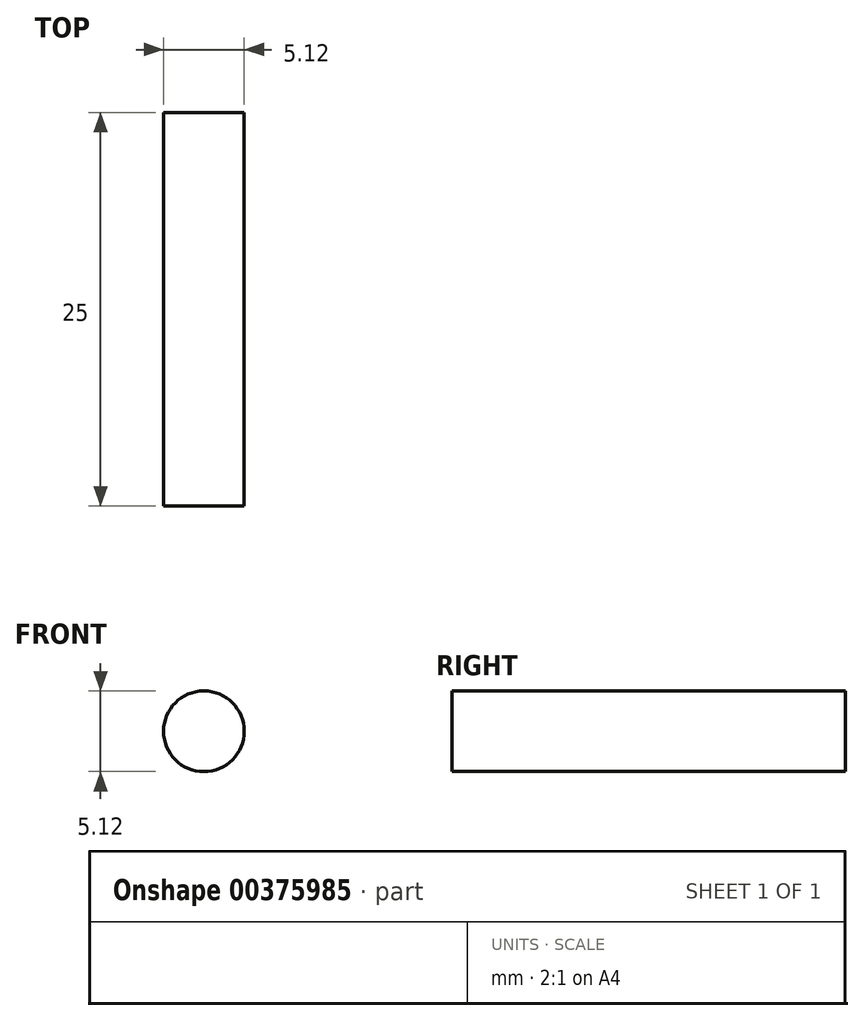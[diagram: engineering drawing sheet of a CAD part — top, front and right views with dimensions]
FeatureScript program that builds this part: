
annotation { "Feature Type Name" : "Feature", "Feature Type Description" : "" }
export const myFeature = defineFeature(function(context is Context, id is Id, definition is map)
    precondition{}
    {
        {
            var Q0;
            Q0=qCreatedBy(makeId("Front.planeOp"),FACE);
            var sketch = newSketch(context, id + "F0", { "sketchPlane" : qUnion([Q0])});
            skCircle(sketch, "E0", {"center": v(0, 0) * mm, "radius": 2.56 * mm});
            skArc(sketch, "E1", {"start": v(-1.68, -4.43) * mm, "mid": v(-2.88, -4.66) * mm, "end": v(-3.9, -5.34) * mm});
            skLineSegment(sketch, "E2", {"start": v(-1.68, -4.42) * mm, "end": v(1.68, -4.42) * mm});
            skArc(sketch, "E3", {"start": v(3.9, -5.34) * mm, "mid": v(2.88, -4.66) * mm, "end": v(1.68, -4.43) * mm});
            skLineSegment(sketch, "E4", {"start": v(3.9, -5.34) * mm, "end": v(7.07, -8.5) * mm});
            skArc(sketch, "E5", {"start": v(6.32, -10.32) * mm, "mid": v(7.3, -9.67) * mm, "end": v(7.07, -8.5) * mm});
            skLineSegment(sketch, "E6", {"start": v(6.32, -10.33) * mm, "end": v(4.22, -10.33) * mm});
            skArc(sketch, "E7", {"start": v(4.22, -10.32) * mm, "mid": v(3.49, -10.63) * mm, "end": v(3.19, -11.36) * mm});
            skLineSegment(sketch, "E8", {"start": v(3.19, -11.36) * mm, "end": v(3.19, -11.47) * mm});
            skArc(sketch, "E9", {"start": v(3.19, -11.47) * mm, "mid": v(3.49, -12.2) * mm, "end": v(4.22, -12.5) * mm});
            skLineSegment(sketch, "E10", {"start": v(4.22, -12.5) * mm, "end": v(5.23, -12.5) * mm});
            skArc(sketch, "E11", {"start": v(6.23, -12.5) * mm, "mid": v(5.73, -12) * mm, "end": v(5.23, -12.5) * mm});
            skLineSegment(sketch, "E12", {"start": v(6.23, -12.5) * mm, "end": v(9.4, -12.5) * mm});
            skArc(sketch, "E13", {"start": v(10.4, -12.5) * mm, "mid": v(9.9, -12) * mm, "end": v(9.4, -12.5) * mm});
            skArc(sketch, "E14", {"start": v(10.4, -12.5) * mm, "mid": v(11.9, -11.9) * mm, "end": v(12.5, -10.4) * mm});
            skArc(sketch, "E15", {"start": v(12.5, -9.4) * mm, "mid": v(12, -9.9) * mm, "end": v(12.5, -10.4) * mm});
            skLineSegment(sketch, "E16", {"start": v(12.5, -9.4) * mm, "end": v(12.5, -6.23) * mm});
            skArc(sketch, "E17", {"start": v(12.5, -5.23) * mm, "mid": v(12, -5.73) * mm, "end": v(12.5, -6.23) * mm});
            skLineSegment(sketch, "E18", {"start": v(12.5, -5.23) * mm, "end": v(12.5, -4.22) * mm});
            skArc(sketch, "E19", {"start": v(12.5, -4.22) * mm, "mid": v(12.2, -3.49) * mm, "end": v(11.47, -3.19) * mm});
            skLineSegment(sketch, "E20", {"start": v(11.47, -3.19) * mm, "end": v(11.36, -3.19) * mm});
            skArc(sketch, "E21", {"start": v(11.36, -3.19) * mm, "mid": v(10.63, -3.49) * mm, "end": v(10.32, -4.22) * mm});
            skLineSegment(sketch, "E22", {"start": v(10.33, -4.22) * mm, "end": v(10.33, -6.3) * mm});
            skArc(sketch, "E23", {"start": v(8.6, -7.02) * mm, "mid": v(9.7, -7.24) * mm, "end": v(10.33, -6.3) * mm});
            skLineSegment(sketch, "E24", {"start": v(8.6, -7.02) * mm, "end": v(5.36, -3.78) * mm});
            skArc(sketch, "E25", {"start": v(4.44, -1.57) * mm, "mid": v(4.68, -2.77) * mm, "end": v(5.36, -3.78) * mm});
            skLineSegment(sketch, "E26", {"start": v(4.44, -1.57) * mm, "end": v(4.44, 1.57) * mm});
            skArc(sketch, "E27", {"start": v(5.36, 3.78) * mm, "mid": v(4.68, 2.77) * mm, "end": v(4.44, 1.57) * mm});
            skLineSegment(sketch, "E28", {"start": v(5.36, 3.78) * mm, "end": v(8.6, 7.02) * mm});
            skArc(sketch, "E29", {"start": v(10.33, 6.3) * mm, "mid": v(9.7, 7.24) * mm, "end": v(8.6, 7.02) * mm});
            skLineSegment(sketch, "E30", {"start": v(10.33, 6.3) * mm, "end": v(10.33, 4.22) * mm});
            skArc(sketch, "E31", {"start": v(10.32, 4.22) * mm, "mid": v(10.63, 3.49) * mm, "end": v(11.36, 3.19) * mm});
            skLineSegment(sketch, "E32", {"start": v(11.36, 3.19) * mm, "end": v(11.47, 3.19) * mm});
            skArc(sketch, "E33", {"start": v(11.47, 3.19) * mm, "mid": v(12.2, 3.49) * mm, "end": v(12.5, 4.22) * mm});
            skLineSegment(sketch, "E34", {"start": v(12.5, 4.22) * mm, "end": v(12.5, 5.23) * mm});
            skArc(sketch, "E35", {"start": v(12.5, 6.23) * mm, "mid": v(12, 5.73) * mm, "end": v(12.5, 5.23) * mm});
            skLineSegment(sketch, "E36", {"start": v(12.5, 6.23) * mm, "end": v(12.5, 9.4) * mm});
            skArc(sketch, "E37", {"start": v(12.5, 10.4) * mm, "mid": v(12, 9.9) * mm, "end": v(12.5, 9.4) * mm});
            skArc(sketch, "E38", {"start": v(12.5, 10.4) * mm, "mid": v(11.9, 11.9) * mm, "end": v(10.4, 12.5) * mm});
            skArc(sketch, "E39", {"start": v(9.4, 12.5) * mm, "mid": v(9.9, 12) * mm, "end": v(10.4, 12.5) * mm});
            skLineSegment(sketch, "E40", {"start": v(9.4, 12.5) * mm, "end": v(6.23, 12.5) * mm});
            skArc(sketch, "E41", {"start": v(5.23, 12.5) * mm, "mid": v(5.73, 12) * mm, "end": v(6.23, 12.5) * mm});
            skLineSegment(sketch, "E42", {"start": v(5.23, 12.5) * mm, "end": v(4.22, 12.5) * mm});
            skArc(sketch, "E43", {"start": v(4.22, 12.5) * mm, "mid": v(3.49, 12.2) * mm, "end": v(3.19, 11.47) * mm});
            skLineSegment(sketch, "E44", {"start": v(3.19, 11.47) * mm, "end": v(3.19, 11.36) * mm});
            skArc(sketch, "E45", {"start": v(3.19, 11.36) * mm, "mid": v(3.49, 10.63) * mm, "end": v(4.22, 10.32) * mm});
            skLineSegment(sketch, "E46", {"start": v(4.22, 10.33) * mm, "end": v(6.37, 10.33) * mm});
            skArc(sketch, "E47", {"start": v(7.1, 8.59) * mm, "mid": v(7.32, 9.7) * mm, "end": v(6.37, 10.32) * mm});
            skLineSegment(sketch, "E48", {"start": v(7.1, 8.59) * mm, "end": v(3.84, 5.34) * mm});
            skArc(sketch, "E49", {"start": v(1.63, 4.43) * mm, "mid": v(2.82, 4.66) * mm, "end": v(3.84, 5.34) * mm});
            skLineSegment(sketch, "E50", {"start": v(1.63, 4.42) * mm, "end": v(-1.63, 4.42) * mm});
            skArc(sketch, "E51", {"start": v(-3.84, 5.34) * mm, "mid": v(-2.82, 4.66) * mm, "end": v(-1.63, 4.43) * mm});
            skLineSegment(sketch, "E52", {"start": v(-3.84, 5.34) * mm, "end": v(-7.1, 8.59) * mm});
            skArc(sketch, "E53", {"start": v(-6.37, 10.32) * mm, "mid": v(-7.32, 9.7) * mm, "end": v(-7.1, 8.59) * mm});
            skLineSegment(sketch, "E54", {"start": v(-6.37, 10.33) * mm, "end": v(-4.22, 10.33) * mm});
            skArc(sketch, "E55", {"start": v(-4.22, 10.32) * mm, "mid": v(-3.49, 10.63) * mm, "end": v(-3.19, 11.36) * mm});
            skLineSegment(sketch, "E56", {"start": v(-3.19, 11.36) * mm, "end": v(-3.19, 11.47) * mm});
            skArc(sketch, "E57", {"start": v(-3.19, 11.47) * mm, "mid": v(-3.49, 12.2) * mm, "end": v(-4.22, 12.5) * mm});
            skLineSegment(sketch, "E58", {"start": v(-4.22, 12.5) * mm, "end": v(-5.23, 12.5) * mm});
            skArc(sketch, "E59", {"start": v(-6.23, 12.5) * mm, "mid": v(-5.73, 12) * mm, "end": v(-5.23, 12.5) * mm});
            skLineSegment(sketch, "E60", {"start": v(-6.23, 12.5) * mm, "end": v(-9.4, 12.5) * mm});
            skArc(sketch, "E61", {"start": v(-10.4, 12.5) * mm, "mid": v(-9.9, 12) * mm, "end": v(-9.4, 12.5) * mm});
            skArc(sketch, "E62", {"start": v(-10.4, 12.5) * mm, "mid": v(-11.9, 11.9) * mm, "end": v(-12.5, 10.4) * mm});
            skArc(sketch, "E63", {"start": v(-12.5, 9.4) * mm, "mid": v(-12, 9.9) * mm, "end": v(-12.5, 10.4) * mm});
            skLineSegment(sketch, "E64", {"start": v(-12.5, 9.4) * mm, "end": v(-12.5, 6.23) * mm});
            skArc(sketch, "E65", {"start": v(-12.5, 5.23) * mm, "mid": v(-12, 5.73) * mm, "end": v(-12.5, 6.23) * mm});
            skLineSegment(sketch, "E66", {"start": v(-12.5, 5.23) * mm, "end": v(-12.5, 4.22) * mm});
            skArc(sketch, "E67", {"start": v(-12.5, 4.22) * mm, "mid": v(-12.2, 3.49) * mm, "end": v(-11.47, 3.19) * mm});
            skLineSegment(sketch, "E68", {"start": v(-11.47, 3.19) * mm, "end": v(-11.36, 3.19) * mm});
            skArc(sketch, "E69", {"start": v(-11.36, 3.19) * mm, "mid": v(-10.63, 3.49) * mm, "end": v(-10.32, 4.22) * mm});
            skLineSegment(sketch, "E70", {"start": v(-10.33, 4.22) * mm, "end": v(-10.33, 6.3) * mm});
            skArc(sketch, "E71", {"start": v(-8.6, 7.02) * mm, "mid": v(-9.7, 7.24) * mm, "end": v(-10.33, 6.3) * mm});
            skLineSegment(sketch, "E72", {"start": v(-8.6, 7.02) * mm, "end": v(-5.36, 3.78) * mm});
            skArc(sketch, "E73", {"start": v(-4.44, 1.57) * mm, "mid": v(-4.68, 2.77) * mm, "end": v(-5.36, 3.78) * mm});
            skLineSegment(sketch, "E74", {"start": v(-4.44, 1.57) * mm, "end": v(-4.44, -1.57) * mm});
            skArc(sketch, "E75", {"start": v(-5.36, -3.78) * mm, "mid": v(-4.68, -2.77) * mm, "end": v(-4.44, -1.57) * mm});
            skLineSegment(sketch, "E76", {"start": v(-5.36, -3.78) * mm, "end": v(-8.6, -7.02) * mm});
            skArc(sketch, "E77", {"start": v(-10.33, -6.3) * mm, "mid": v(-9.7, -7.24) * mm, "end": v(-8.6, -7.02) * mm});
            skLineSegment(sketch, "E78", {"start": v(-10.33, -6.3) * mm, "end": v(-10.33, -4.22) * mm});
            skArc(sketch, "E79", {"start": v(-10.32, -4.22) * mm, "mid": v(-10.63, -3.49) * mm, "end": v(-11.36, -3.19) * mm});
            skLineSegment(sketch, "E80", {"start": v(-11.36, -3.19) * mm, "end": v(-11.47, -3.19) * mm});
            skArc(sketch, "E81", {"start": v(-11.47, -3.19) * mm, "mid": v(-12.2, -3.49) * mm, "end": v(-12.5, -4.22) * mm});
            skLineSegment(sketch, "E82", {"start": v(-12.5, -4.22) * mm, "end": v(-12.5, -5.23) * mm});
            skArc(sketch, "E83", {"start": v(-12.5, -6.23) * mm, "mid": v(-12, -5.73) * mm, "end": v(-12.5, -5.23) * mm});
            skLineSegment(sketch, "E84", {"start": v(-12.5, -6.23) * mm, "end": v(-12.5, -9.4) * mm});
            skArc(sketch, "E85", {"start": v(-12.5, -10.4) * mm, "mid": v(-12, -9.9) * mm, "end": v(-12.5, -9.4) * mm});
            skArc(sketch, "E86", {"start": v(-12.5, -10.4) * mm, "mid": v(-11.9, -11.9) * mm, "end": v(-10.4, -12.5) * mm});
            skArc(sketch, "E87", {"start": v(-9.4, -12.5) * mm, "mid": v(-9.9, -12) * mm, "end": v(-10.4, -12.5) * mm});
            skLineSegment(sketch, "E88", {"start": v(-9.4, -12.5) * mm, "end": v(-6.23, -12.5) * mm});
            skArc(sketch, "E89", {"start": v(-5.23, -12.5) * mm, "mid": v(-5.73, -12) * mm, "end": v(-6.23, -12.5) * mm});
            skLineSegment(sketch, "E90", {"start": v(-5.23, -12.5) * mm, "end": v(-4.22, -12.5) * mm});
            skArc(sketch, "E91", {"start": v(-4.22, -12.5) * mm, "mid": v(-3.49, -12.2) * mm, "end": v(-3.19, -11.47) * mm});
            skLineSegment(sketch, "E92", {"start": v(-3.19, -11.47) * mm, "end": v(-3.19, -11.36) * mm});
            skArc(sketch, "E93", {"start": v(-3.19, -11.36) * mm, "mid": v(-3.49, -10.63) * mm, "end": v(-4.22, -10.32) * mm});
            skLineSegment(sketch, "E94", {"start": v(-4.22, -10.33) * mm, "end": v(-6.32, -10.33) * mm});
            skArc(sketch, "E95", {"start": v(-7.07, -8.5) * mm, "mid": v(-7.3, -9.67) * mm, "end": v(-6.32, -10.32) * mm});
            skLineSegment(sketch, "E96", {"start": v(-7.07, -8.5) * mm, "end": v(-3.9, -5.34) * mm});
            skSolve(sketch);
        }
        {
            var Q0;
            Q0=makeQuery(id+"F0.imprint","IMPRINT",FACE,{"disambiguationData":[TD([[makeQuery(id+"F0.imprint","IMPRINT",EDGE,{"derivedFrom":sQuery(id+"F0.wireOp",EDGE,"E0")}),1.0]])]});
            extrude(context, id + "F1", {"entities" : qUnion([Q0]), "endBound" : BoundingType.SYMMETRIC, "depth" : 25 * mm});
        }
        {
            var Q0;
            Q0=qCreatedBy(makeId("Front.planeOp"),FACE);
            var sketch = newSketch(context, id + "F2", { "sketchPlane" : qUnion([Q0])});
            skCircle(sketch, "E97", {"center": v(0, 0) * mm, "radius": 17.68 * mm});
            skCircle(sketch, "E98", {"center": v(0, 0) * mm, "radius": 47.67 * mm});
            skSolve(sketch);
        }
        {
            var Q0;
            Q0=qSketchRegion(id+"F2",true);
            var Q1;
            Q1=makeQuery(id+"F2.imprint","IMPRINT",FACE,{"disambiguationData":[TD([[makeQuery(id+"F2.imprint","IMPRINT",EDGE,{"derivedFrom":sQuery(id+"F2.wireOp",EDGE,"E97")}),1.0]])]});
            extrude(context, id + "F3", {"entities" : qUnion([Q0, Q1]), "endBound" : BoundingType.SYMMETRIC, "depth" : 5 * mm});
        }
        {
            var Q0;
            Q0=qSketchRegion(id+"F0",true);
            extrude(context, id + "F4", {"entities" : qUnion([Q0]), "operationType" : NewBodyOperationType.REMOVE, "endBound" : BoundingType.SYMMETRIC, "oppositeDirection" : true, "depth" : 25 * mm});
        }
        {
            var Q0;
            Q0=makeQuery(id+"F4.boolean.opBoolean","SPLIT",BODY,{"disambiguationData":[OD(1.0)],"derivedFrom":makeQuery(id+"F3.opExtrude","SWEPT_BODY",BODY,{"disambiguationData":[OSD([sQuery(id+"F2.wireOp",EDGE,"E98")])]})});
            deleteBodies(context, id + "F5", {"entities" : qUnion([Q0])});
        }
    });
